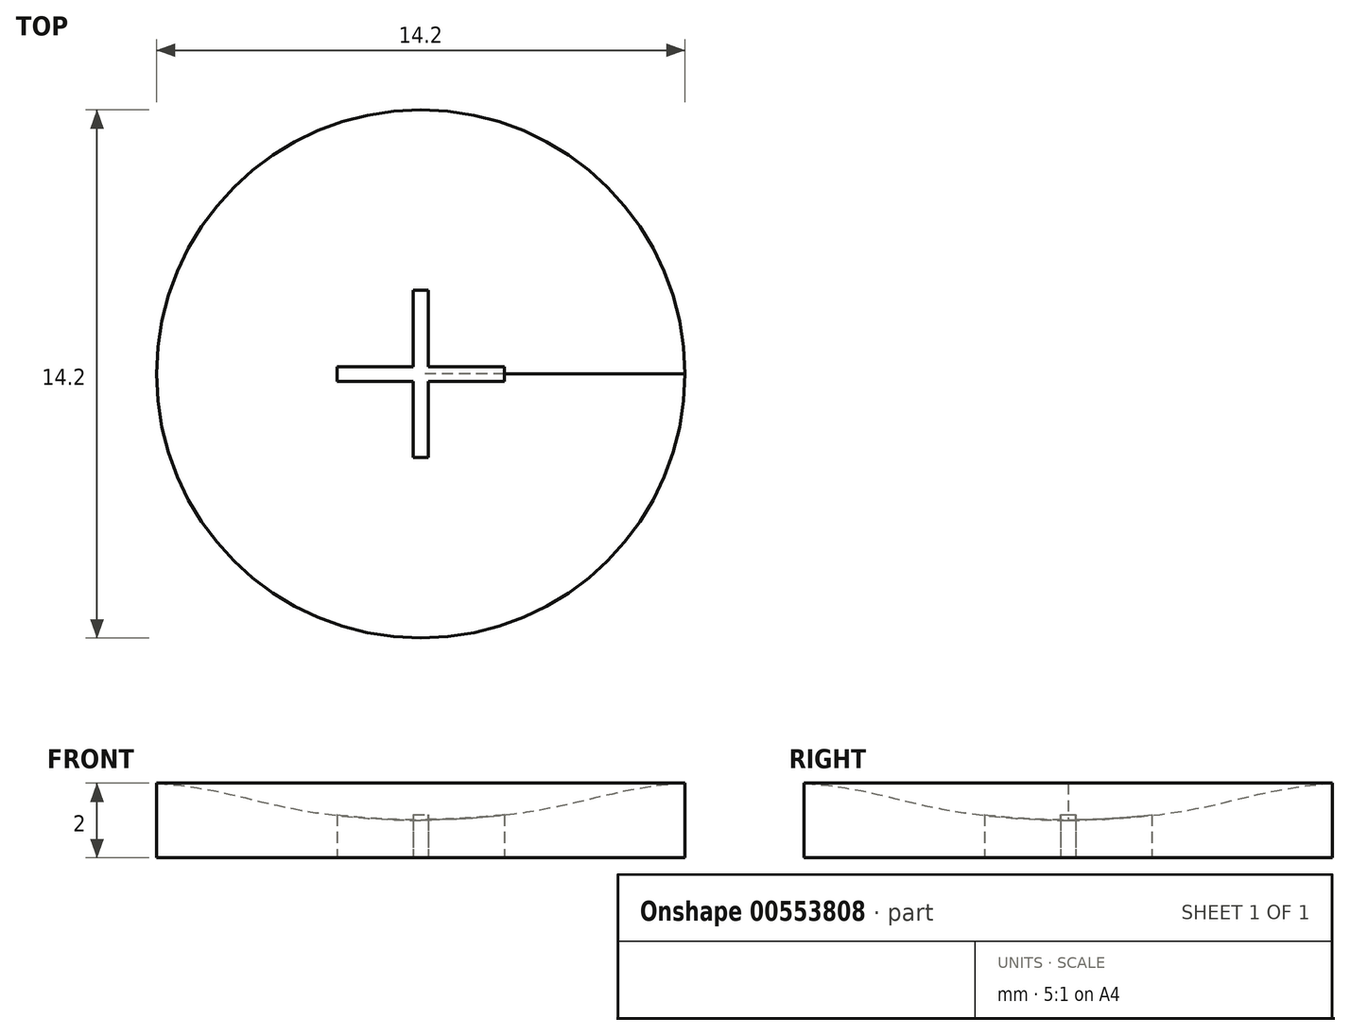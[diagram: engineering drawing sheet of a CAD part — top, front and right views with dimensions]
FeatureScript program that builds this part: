
annotation { "Feature Type Name" : "Feature", "Feature Type Description" : "" }
export const myFeature = defineFeature(function(context is Context, id is Id, definition is map)
    precondition{}
    {
        {
            var Q0;
            Q0=qCreatedBy(makeId("Front.planeOp"),FACE);
            var sketch = newSketch(context, id + "F0", { "sketchPlane" : qUnion([Q0])});
            skLineSegment(sketch, "E0", {"start": v(0, 0) * mm, "end": v(7.1, 0) * mm});
            skLineSegment(sketch, "E1", {"start": v(7.1, 0) * mm, "end": v(7.1, 2) * mm});
            skLineSegment(sketch, "E2", {"start": v(0, 1) * mm, "end": v(0, 0) * mm});
            skFitSpline(sketch, "E3", {"points": [v(7.1, 2) * mm, v(0, 1) * mm], "startDerivative": vector(-7.89, -0.57) * mm, "endDerivative": vector(-12, -0.18) * mm});
            skPoint(sketch, "E4.orphan", {"position": v(0, 2) * mm});
            skSolve(sketch);
        }
        {
            var Q0;
            Q0=makeQuery(id+"F0.imprint","IMPRINT",FACE,{"disambiguationData":[TD([[makeQuery(id+"F0.imprint","IMPRINT",EDGE,{"derivedFrom":sQuery(id+"F0.wireOp",EDGE,"E0")}),1.0]])]});
            var Q1;
            Q1=sQuery(id+"F0.wireOp",EDGE,"E2");
            revolve(context, id + "F1", {"entities" : qUnion([Q0]), "axis" : qUnion([Q1]), "revolveType" : RevolveType.FULL});
        }
        {
            var Q0;
            Q0=makeQuery(id+"F1.opRevolve","SWEPT_FACE",FACE,{"disambiguationData":[OSD([sQuery(id+"F0.wireOp",EDGE,"E0")])]});
            var sketch = newSketch(context, id + "F2", { "sketchPlane" : qUnion([Q0])});
            skLineSegment(sketch, "E5.bottom", {"start": v(0.2, -2.25) * mm, "end": v(-0.2, -2.25) * mm});
            skLineSegment(sketch, "E5.top", {"start": v(0.2, 2.25) * mm, "end": v(-0.2, 2.25) * mm});
            skLineSegment(sketch, "E5.left", {"start": v(0.2, -2.25) * mm, "end": v(0.2, -0.2) * mm});
            skLineSegment(sketch, "E5.right", {"start": v(-0.2, -2.25) * mm, "end": v(-0.2, -0.2) * mm});
            skPoint(sketch, "E5.middle", {"position": v(0, 0) * mm});
            skLineSegment(sketch, "E6.bottom", {"start": v(2.25, -0.2) * mm, "end": v(0.2, -0.2) * mm});
            skLineSegment(sketch, "E6.top", {"start": v(2.25, 0.2) * mm, "end": v(0.2, 0.2) * mm});
            skLineSegment(sketch, "E6.left", {"start": v(2.25, -0.2) * mm, "end": v(2.25, 0.2) * mm});
            skLineSegment(sketch, "E6.right", {"start": v(-2.25, -0.2) * mm, "end": v(-2.25, 0.2) * mm});
            skLineSegment(sketch, "E7.trimOffspring", {"start": v(-0.2, 0.2) * mm, "end": v(-2.25, 0.2) * mm});
            skLineSegment(sketch, "E8.trimOffspring", {"start": v(-0.2, 0.2) * mm, "end": v(-0.2, 2.25) * mm});
            skLineSegment(sketch, "E9.trimOffspring", {"start": v(-0.2, -0.2) * mm, "end": v(-2.25, -0.2) * mm});
            skLineSegment(sketch, "E10.trimOffspring", {"start": v(0.2, 0.2) * mm, "end": v(0.2, 2.25) * mm});
            skSolve(sketch);
        }
        {
            var Q0;
            Q0=makeQuery(id+"F2.imprint","IMPRINT",FACE,{"disambiguationData":[TD([[makeQuery(id+"F2.imprint","IMPRINT",EDGE,{"derivedFrom":sQuery(id+"F2.wireOp",EDGE,"E5.bottom")}),-1.0]])]});
            extrude(context, id + "F3", {"entities" : qUnion([Q0]), "endBound" : BoundingType.UP_TO_NEXT, "oppositeDirection" : true, "depth" : 25 * mm, "hasOffset" : true, "offsetDistance" : 0.02 * mm, "offsetOppositeDirection" : true});
        }
    });
